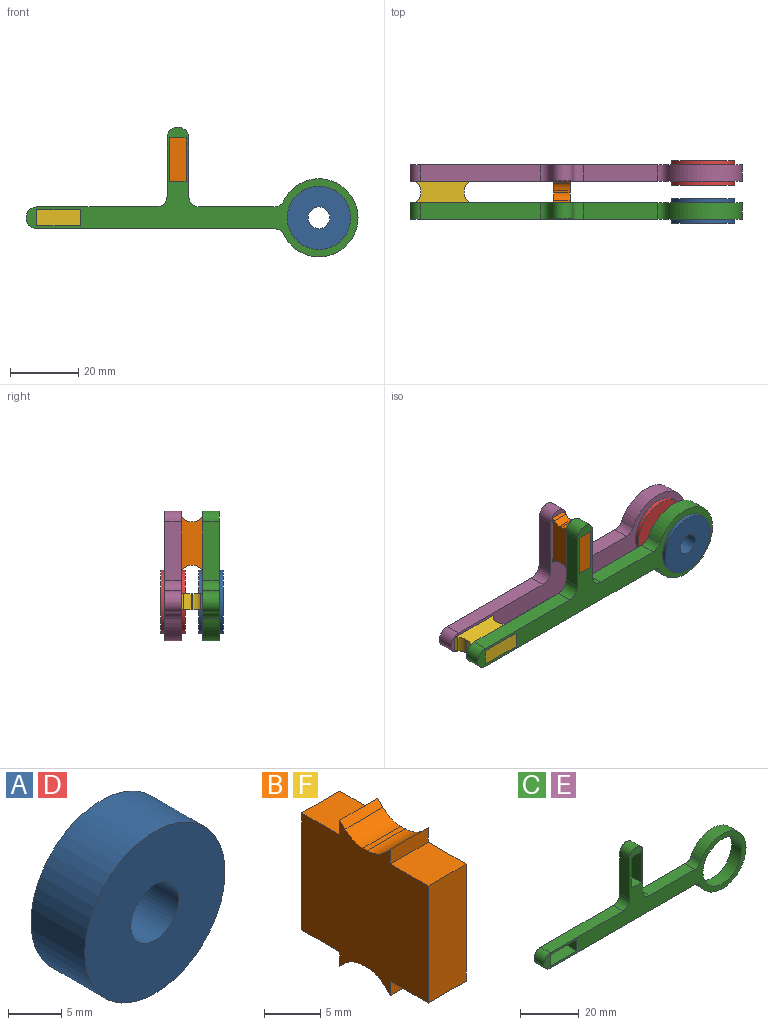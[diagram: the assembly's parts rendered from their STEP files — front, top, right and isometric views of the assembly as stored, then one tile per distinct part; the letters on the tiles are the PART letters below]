
ASSEMBLY  parts=6 mates=5
PART A: 4 faces, bbox 18.5x7.1x18.5 mm
  f0: cylinder r=3.17mm len=7.11mm, axis (0,1,0), area 141.9mm2, adj f2,f3
  f1: cylinder r=9.27mm len=18.54mm, axis (0,1,0), area 414.3mm2, adj f2,f3
  f2: plane 18.54x18.54mm, normal (0,-1,0), area 238.4mm2, adj f0,f1
  f3: plane 18.54x18.54mm, normal (0,1,0), area 238.4mm2, adj f0,f1
PART B: 22 faces, bbox 4.8x15.9x15.9 mm
  f0: plane 4.76x4.76mm, normal (0,0,1), area 22.7mm2, adj f1,f19,f20,f21
  f1: plane 4.76x1.59mm, normal (0,1,0), area 7.6mm2, adj f0,f2,f20,f21
  f2: plane 4.76x0.66mm, normal (0,-0.71,0.71), area 4.4mm2, adj f1,f3,f20,f21
  f3: cylinder r=3.17mm len=4.76mm, axis (-1,0,0), area 11.9mm2, adj f2,f4,f20,f21
  f4: plane 4.76x0.54mm, normal (0,0,1), area 2.6mm2, adj f3,f5,f20,f21
  f5: cylinder r=3.17mm len=4.76mm, axis (-1,0,0), area 11.9mm2, adj f4,f6,f20,f21
  f6: plane 4.76x0.66mm, normal (0,0.71,0.71), area 4.4mm2, adj f5,f7,f20,f21
  f7: plane 4.76x1.59mm, normal (0,-1,0), area 7.6mm2, adj f6,f8,f20,f21
  f8: plane 4.76x4.76mm, normal (0,0,1), area 22.7mm2, adj f7,f9,f20,f21
  f9: plane 12.7x4.76mm, normal (0,-1,0), area 60.5mm2, adj f8,f10,f20,f21
  f10: plane 4.76x4.76mm, normal (0,0,-1), area 22.7mm2, adj f9,f11,f20,f21
  f11: plane 4.76x1.59mm, normal (0,-1,0), area 7.6mm2, adj f10,f12,f20,f21
  f12: plane 4.76x0.66mm, normal (0,0.71,-0.71), area 4.4mm2, adj f11,f13,f20,f21
  f13: cylinder r=3.17mm len=4.76mm, axis (-1,0,0), area 11.9mm2, adj f12,f14,f20,f21
  f14: plane 4.76x0.54mm, normal (0,0,-1), area 2.6mm2, adj f13,f15,f20,f21
  f15: cylinder r=3.17mm len=4.76mm, axis (-1,0,0), area 11.9mm2, adj f14,f16,f20,f21
  f16: plane 4.76x0.66mm, normal (0,-0.71,-0.71), area 4.4mm2, adj f15,f17,f20,f21
  f17: plane 4.76x1.59mm, normal (0,1,0), area 7.6mm2, adj f16,f18,f20,f21
  f18: plane 4.76x4.76mm, normal (0,0,-1), area 22.7mm2, adj f17,f19,f20,f21
  f19: plane 12.7x4.76mm, normal (0,1,0), area 60.5mm2, adj f0,f18,f20,f21
  f20: plane 15.88x15.88mm, normal (1,0,0), area 207.5mm2, adj f0,f1,f2,f3,f4,f5,f6,f7
  f21: plane 15.88x15.88mm, normal (-1,0,0), area 207.5mm2, adj f0,f1,f2,f3,f4,f5,f6,f7
PART C: 23 faces, bbox 97.2x4.8x38 mm
  f0: plane 97.16x37.97mm, normal (0,-1,0), area 637.8mm2, adj f2,f3,f4,f5,f6,f7,f8,f9
  f1: plane 97.16x37.97mm, normal (0,1,0), area 637.8mm2, adj f2,f3,f4,f5,f6,f7,f8,f9
  f2: cylinder r=3.17mm len=4.76mm, axis (0,1,0), area 23.8mm2, adj f0,f1,f3,f13
  f3: plane 34.93x4.76mm, normal (0,0,1), area 166.3mm2, adj f0,f1,f2,f4
  f4: cylinder r=3.17mm len=6.35mm, axis (0,1,0), area 47.5mm2, adj f0,f1,f3,f5
  f5: plane 69.4x4.76mm, normal (0,0,-1), area 330.5mm2, adj f0,f1,f4,f6
  f6: cylinder r=3.17mm len=4.76mm, axis (0,1,0), area 17mm2, adj f0,f1,f5,f7
  f7: cylinder r=11.43mm len=22.86mm, axis (0,1,0), area 293.1mm2, adj f0,f1,f6,f8
  f8: cylinder r=3.17mm len=4.76mm, axis (0,1,0), area 17mm2, adj f0,f1,f7,f9
  f9: plane 21.77x4.76mm, normal (0,0,1), area 103.7mm2, adj f0,f1,f8,f10
  f10: cylinder r=3.17mm len=4.76mm, axis (0,1,0), area 23.8mm2, adj f0,f1,f9,f11
  f11: plane 17.02x4.76mm, normal (1,0,0), area 81mm2, adj f0,f1,f10,f12
  f12: cylinder r=3.17mm len=6.35mm, axis (0,1,0), area 47.5mm2, adj f0,f1,f11,f13
  f13: plane 17.02x4.76mm, normal (-1,0,0), area 81mm2, adj f0,f1,f2,f12
  f14: cylinder r=9.27mm len=18.54mm, axis (0,1,0), area 277.4mm2, adj f0,f1
  f15: plane 12.7x4.76mm, normal (0,0,-1), area 60.5mm2, adj f0,f1,f16,f18
  f16: plane 4.76x4.76mm, normal (1,0,0), area 22.7mm2, adj f0,f1,f15,f17
  f17: plane 12.7x4.76mm, normal (0,0,1), area 60.5mm2, adj f0,f1,f16,f18
  f18: plane 4.76x4.76mm, normal (-1,0,0), area 22.7mm2, adj f0,f1,f15,f17
  f19: plane 4.76x4.76mm, normal (0,0,-1), area 22.7mm2, adj f0,f1,f20,f22
  f20: plane 12.7x4.76mm, normal (1,0,0), area 60.5mm2, adj f0,f1,f19,f21
  f21: plane 4.76x4.76mm, normal (0,0,1), area 22.7mm2, adj f0,f1,f20,f22
  f22: plane 12.7x4.76mm, normal (-1,0,0), area 60.5mm2, adj f0,f1,f19,f21
PART D: same geometry as A
PART E: same geometry as C
PART F: same geometry as B
PLACE A t=(64.74,-10.91,34.11)mm
PLACE B t=(21.08,-16.85,51.13)mm
PLACE C t=(23.46,-12.08,34.11)mm
PLACE D t=(64.74,0.2,34.11)mm
PLACE E t=(23.46,-0.97,34.11)mm
PLACE F rot(axis=(0,-1,0),90deg) t=(-11.46,-16.85,31.73)mm
MATE fastened A.f1 <-> C.f14  axis (0,1,0) through (64.74,-14.46,34.11)mm
MATE fastened F.f20 <-> C.f15  axis (0,0,1) through (-11.46,-16.85,36.49)mm
MATE fastened E.f14 <-> D.f1  axis (0,1,0) through (64.74,-3.35,34.11)mm
MATE fastened E.f12 <-> B.f1  axis (0,-1,0) through (23.46,-5.73,57.48)mm
MATE fastened B.f7 <-> C.f12  axis (0,-1,0) through (23.46,-12.08,57.48)mm
